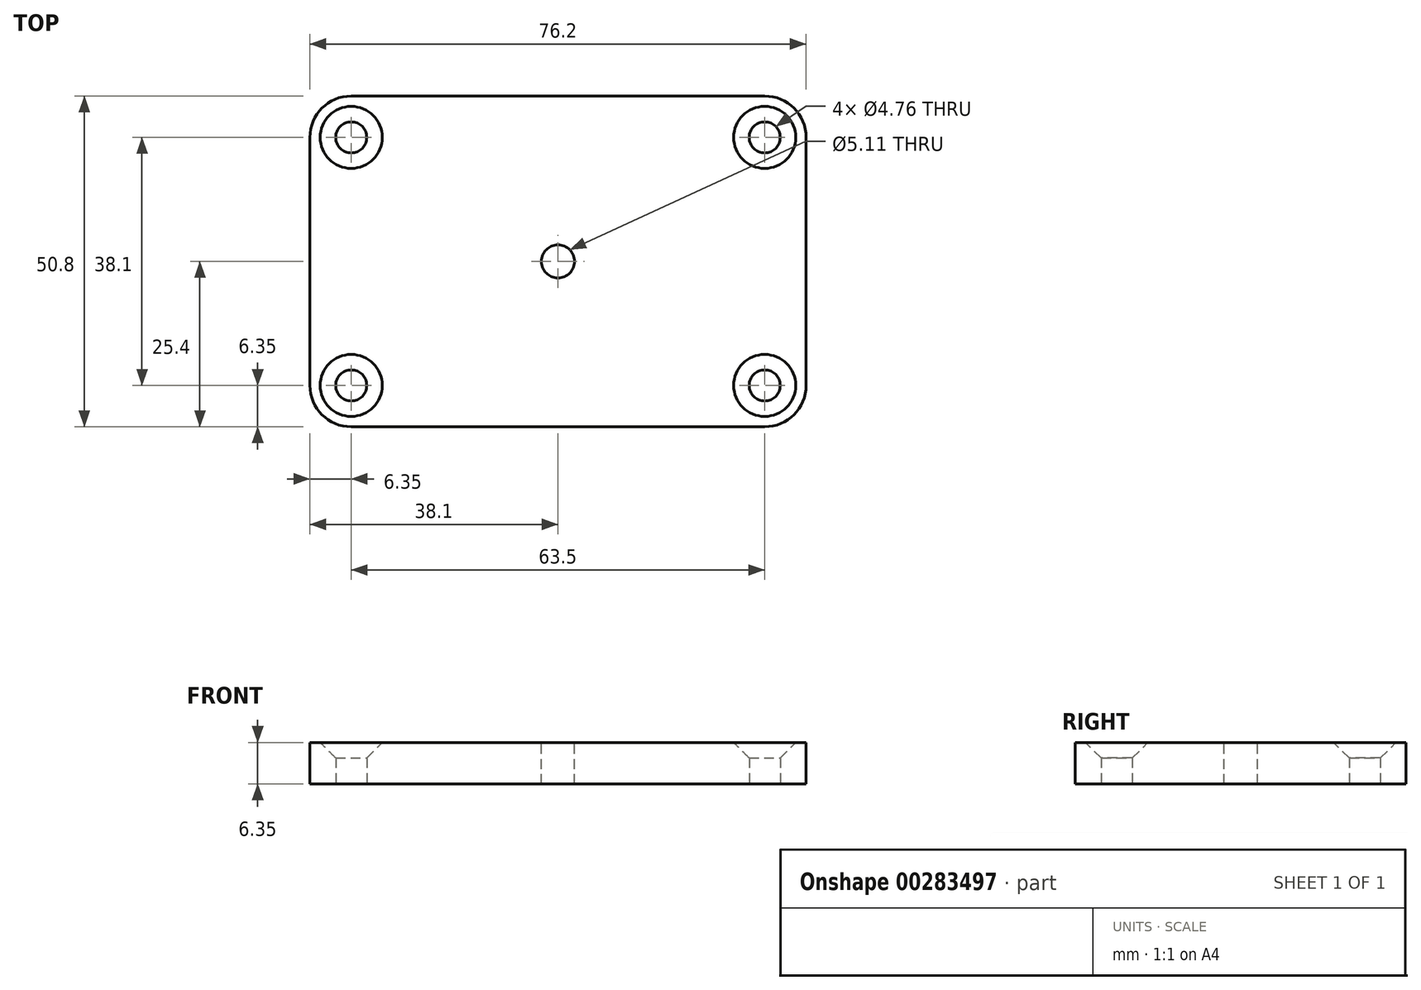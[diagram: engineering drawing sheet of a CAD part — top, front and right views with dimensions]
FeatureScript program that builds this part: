
annotation { "Feature Type Name" : "Feature", "Feature Type Description" : "" }
export const myFeature = defineFeature(function(context is Context, id is Id, definition is map)
    precondition{}
    {
        {
            var Q0;
            Q0=qCreatedBy(makeId("Top.planeOp"),FACE);
            var sketch = newSketch(context, id + "F0", { "sketchPlane" : qUnion([Q0])});
            skCircle(sketch, "E0", {"center": v(0, 0) * mm, "radius": 41.28 * mm, "construction": true});
            skCircle(sketch, "E1.0", {"center": v(0, 0) * mm, "radius": 34.93 * mm, "construction": true});
            skLineSegment(sketch, "E2", {"start": v(-7.63, -34.08) * mm, "end": v(0, 0) * mm, "construction": true});
            skLineSegment(sketch, "E3", {"start": v(0, 0) * mm, "end": v(30.94, -16.2) * mm, "construction": true});
            skLineSegment(sketch, "E4", {"start": v(40.64, 50.8) * mm, "end": v(-86.34, 52.78) * mm});
            skLineSegment(sketch, "E5", {"start": v(30.94, -16.2) * mm, "end": v(39.13, -133.7) * mm});
            skCircle(sketch, "E6", {"center": v(40.64, 50.8) * mm, "radius": 101.6 * mm, "construction": true});
            skLineSegment(sketch, "E7", {"start": v(-60.95, 52.39) * mm, "end": v(-60.95, 52.39) * mm});
            skLineSegment(sketch, "E8", {"start": v(-10.35, 38.9) * mm, "end": v(-7.63, -34.08) * mm, "construction": true});
            skCircle(sketch, "E9.0", {"center": v(0, 0) * mm, "radius": 28.57 * mm, "construction": true});
            skCircle(sketch, "E10.0", {"center": v(40.64, 50.8) * mm, "radius": 100.93 * mm});
            skLineSegment(sketch, "E11.0", {"start": v(5.89, 11.25) * mm, "end": v(36.83, -4.94) * mm});
            skLineSegment(sketch, "E12.0", {"start": v(-20.03, -31.3) * mm, "end": v(-12.4, 2.78) * mm});
            skLineSegment(sketch, "E13", {"start": v(-7.63, -34.08) * mm, "end": v(30.94, -16.2) * mm, "construction": true});
            skLineSegment(sketch, "E14.0", {"start": v(-2.3, -45.6) * mm, "end": v(36.28, -27.72) * mm});
            skArc(sketch, "E15.filletArc", {"start": v(-20.03, -31.3) * mm, "mid": v(-15.6, -43.97) * mm, "end": v(-2.3, -45.6) * mm});
            skArc(sketch, "E16.filletArc", {"start": v(36.28, -27.72) * mm, "mid": v(43.64, -16.5) * mm, "end": v(36.83, -4.94) * mm});
            skArc(sketch, "E17.filletArc", {"start": v(5.89, 11.25) * mm, "mid": v(-5.34, 11.52) * mm, "end": v(-12.4, 2.78) * mm});
            skCircle(sketch, "E18", {"center": v(0, 0) * mm, "radius": 6.35 * mm});
            skCircle(sketch, "E19", {"center": v(-7.63, -34.08) * mm, "radius": 3.18 * mm});
            skCircle(sketch, "E20", {"center": v(30.94, -16.2) * mm, "radius": 6.35 * mm});
            skLineSegment(sketch, "E21", {"start": v(-10.15, 51.6) * mm, "end": v(-10.35, 38.9) * mm});
            skCircle(sketch, "E22", {"center": v(-10.35, 38.9) * mm, "radius": 3.18 * mm});
            skArc(sketch, "E23", {"start": v(-10.35, 38.9) * mm, "mid": v(-18.3, 2.06) * mm, "end": v(-7.63, -34.08) * mm, "construction": true});
            skArc(sketch, "E24.0", {"start": v(-4.67, 36.06) * mm, "mid": v(-7.52, 44.58) * mm, "end": v(-16.03, 41.73) * mm});
            skArc(sketch, "E25.0", {"start": v(-16.03, 41.73) * mm, "mid": v(-24.65, 1.82) * mm, "end": v(-13.1, -37.33) * mm});
            skArc(sketch, "E26.0", {"start": v(-4.67, 36.06) * mm, "mid": v(-11.96, 2.3) * mm, "end": v(-2.18, -30.83) * mm});
            skArc(sketch, "E27.0", {"start": v(-13.1, -37.33) * mm, "mid": v(-4.39, -39.54) * mm, "end": v(-2.18, -30.83) * mm});
            skSolve(sketch);
        }
        {
            var Q0;
            Q0=qCreatedBy(makeId("Top.planeOp"),FACE);
            var sketch = newSketch(context, id + "F1", { "sketchPlane" : qUnion([Q0])});
            skLineSegment(sketch, "E28.bottom", {"start": v(-38.1, 25.4) * mm, "end": v(38.1, 25.4) * mm});
            skLineSegment(sketch, "E28.top", {"start": v(-38.1, -25.4) * mm, "end": v(38.1, -25.4) * mm});
            skLineSegment(sketch, "E28.left", {"start": v(-38.1, 25.4) * mm, "end": v(-38.1, -25.4) * mm});
            skLineSegment(sketch, "E28.right", {"start": v(38.1, 25.4) * mm, "end": v(38.1, -25.4) * mm});
            skSolve(sketch);
        }
        {
            var Q0;
            Q0 = qSketchRegion(id + "F1", true);
            extrude(context, id + "F2", {"entities" : qUnion([Q0]), "depth" : 6.35 * mm});
        }
        {
            var Q0;
            Q0=makeQuery(id+"F2.opExtrude","SWEPT_EDGE",EDGE,{"disambiguationData":[OSD([sQuery(id+"F1.wireOp",EDGE,"E28.top"),sQuery(id+"F1.wireOp",EDGE,"E28.left")])]});
            var Q1;
            Q1=makeQuery(id+"F2.opExtrude","SWEPT_EDGE",EDGE,{"disambiguationData":[OSD([sQuery(id+"F1.wireOp",EDGE,"E28.top"),sQuery(id+"F1.wireOp",EDGE,"E28.right")])]});
            var Q2;
            Q2=makeQuery(id+"F2.opExtrude","SWEPT_EDGE",EDGE,{"disambiguationData":[OSD([sQuery(id+"F1.wireOp",EDGE,"E28.bottom"),sQuery(id+"F1.wireOp",EDGE,"E28.right")])]});
            var Q3;
            Q3=makeQuery(id+"F2.opExtrude","SWEPT_EDGE",EDGE,{"disambiguationData":[OSD([sQuery(id+"F1.wireOp",EDGE,"E28.bottom"),sQuery(id+"F1.wireOp",EDGE,"E28.left")])]});
            fillet(context, id + "F3", {"entities" : qUnion([Q0, Q1, Q2, Q3]), "radius" : 6.35 * mm, "tangentPropagation" : true, "allowEdgeOverflow" : false});
        }
        {
            var Q0;
            Q0=makeQuery(id+"F2.opExtrude","CAP_FACE",FACE,{"disambiguationData":[OSD([sQuery(id+"F1.wireOp",EDGE,"E28.bottom"),sQuery(id+"F1.wireOp",EDGE,"E28.top"),sQuery(id+"F1.wireOp",EDGE,"E28.left"),sQuery(id+"F1.wireOp",EDGE,"E28.right")])],"isStart":false});
            var sketch = newSketch(context, id + "F4", { "sketchPlane" : qUnion([Q0])});
            skPoint(sketch, "E29", {"position": v(-31.75, 19.05) * mm});
            skPoint(sketch, "E30", {"position": v(-31.75, -19.05) * mm});
            skPoint(sketch, "E31", {"position": v(31.75, -19.05) * mm});
            skPoint(sketch, "E32", {"position": v(31.75, 19.05) * mm});
            skSolve(sketch);
        }
        {
            var Q0;
            Q0=sQuery(id+"F4.wireOp",VERTEX,"E29");
            var Q1;
            Q1=sQuery(id+"F4.wireOp",VERTEX,"E30");
            var Q2;
            Q2=sQuery(id+"F4.wireOp",VERTEX,"E31");
            var Q3;
            Q3=sQuery(id+"F4.wireOp",VERTEX,"E32");
            var Q4;
            Q4=makeQuery(id+"F2.opExtrude","SWEPT_BODY",BODY,{"disambiguationData":[OSD([sQuery(id+"F1.wireOp",EDGE,"E28.bottom"),sQuery(id+"F1.wireOp",EDGE,"E28.top"),sQuery(id+"F1.wireOp",EDGE,"E28.left"),sQuery(id+"F1.wireOp",EDGE,"E28.right")])]});
            hole(context, id + "F5", {"style" : HoleStyle.C_SINK, "endStyle" : HoleEndStyle.THROUGH, "holeDiameter" : 4.76 * mm, "cSinkDiameter" : 9.52 * mm, "cSinkAngle" : 90 * degree, "tappedDepth" : 12.7 * mm, "tapClearance" : 3, "locations" : qUnion([Q0, Q1, Q2, Q3]), "scope" : qUnion([Q4])});
        }
        {
            var Q0;
            Q0=sQuery(id+"F0.wireOp",VERTEX,"E9.0.center");
            var Q1;
            Q1=makeQuery(id+"F2.opExtrude","SWEPT_BODY",BODY,{"disambiguationData":[OSD([sQuery(id+"F1.wireOp",EDGE,"E28.bottom"),sQuery(id+"F1.wireOp",EDGE,"E28.top"),sQuery(id+"F1.wireOp",EDGE,"E28.left"),sQuery(id+"F1.wireOp",EDGE,"E28.right")])]});
            hole(context, id + "F6", {"style" : HoleStyle.SIMPLE, "endStyle" : HoleEndStyle.THROUGH, "oppositeDirection" : true, "standardTappedOrClearance" : lookupTablePath({ "standard" : "ANSI", "engagement" : "75%", "pitch" : "20 tpi", "size" : "1/4", "type" : "Tapped" }), "standardBlindInLast" : lookupTablePath({ "standard" : "ANSI", "engagement" : "75%", "pitch" : "20 tpi", "size" : "1/4", "type" : "Tapped" }), "holeDiameter" : 5.1 * mm, "showTappedDepth" : true, "tappedDepth" : 12.7 * mm, "tapClearance" : 3, "locations" : qUnion([Q0]), "scope" : qUnion([Q1]), "majorDiameter" : 6.35 * mm});
        }
    });
